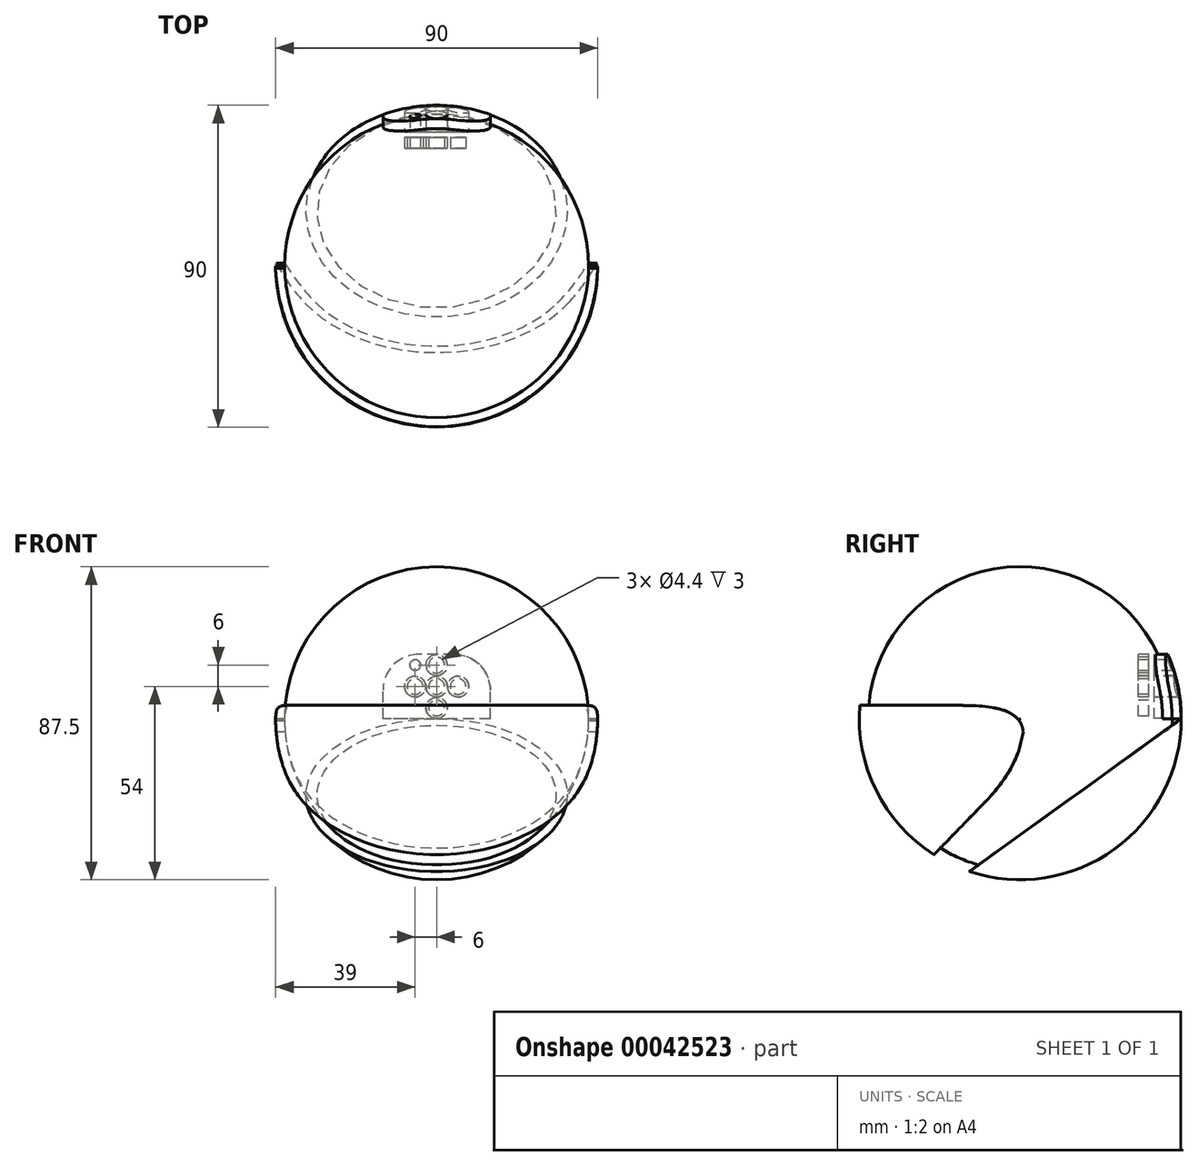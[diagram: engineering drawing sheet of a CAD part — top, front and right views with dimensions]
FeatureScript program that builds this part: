
annotation { "Feature Type Name" : "Feature", "Feature Type Description" : "" }
export const myFeature = defineFeature(function(context is Context, id is Id, definition is map)
    precondition{}
    {
        {
            var Q0;
            Q0=qCreatedBy(makeId("Right.planeOp"),FACE);
            var sketch = newSketch(context, id + "F0", { "sketchPlane" : qUnion([Q0])});
            skArc(sketch, "E0", {"start": v(40, 0) * mm, "mid": v(38.33, 11.42) * mm, "end": v(33.48, 21.9) * mm});
            skLineSegment(sketch, "E1", {"start": v(0, -40) * mm, "end": v(0, 40) * mm, "construction": true});
            skLineSegment(sketch, "E2", {"start": v(-40, 0) * mm, "end": v(40, 0) * mm, "construction": true});
            skPoint(sketch, "E3", {"position": v(33.48, 21.9) * mm});
            skPoint(sketch, "E4", {"position": v(-21.9, -33.48) * mm});
            skLineSegment(sketch, "E5", {"start": v(-21.9, -33.48) * mm, "end": v(33.48, 21.9) * mm, "construction": true});
            skPoint(sketch, "E6", {"position": v(12.26, 0.68) * mm});
            skPoint(sketch, "E7", {"position": v(-7.75, -19.33) * mm});
            skFitSpline(sketch, "E8", {"points": [v(-7.75, -19.33) * mm, v(4.22, 8.7) * mm], "startDerivative": vector(26.03, 26.03) * mm, "endDerivative": vector(-1.06, 47.13) * mm});
            skFitSpline(sketch, "E9", {"points": [v(33.48, 21.9) * mm, v(12.36, 15.68) * mm], "startDerivative": vector(-15.28, -15.28) * mm, "endDerivative": vector(-38.84, 5.85) * mm});
            skArc(sketch, "E10.trimOffspring", {"start": v(20.07, 15.1) * mm, "mid": v(11.15, 14.38) * mm, "end": v(4.22, 8.7) * mm});
            skLineSegment(sketch, "E11", {"start": v(33.48, 21.9) * mm, "end": v(40, 21.9) * mm});
            skLineSegment(sketch, "E12", {"start": v(40, 0) * mm, "end": v(40, 21.9) * mm});
            skCircle(sketch, "E13", {"center": v(0, 0) * mm, "radius": 40 * mm, "construction": true});
            skPoint(sketch, "E14", {"position": v(0, -32.17) * mm});
            skPoint(sketch, "E15", {"position": v(40, 0) * mm});
            skLineSegment(sketch, "E16", {"start": v(-21.9, -33.48) * mm, "end": v(-14.82, -40.55) * mm});
            skLineSegment(sketch, "E17", {"start": v(-14.82, -40.55) * mm, "end": v(40, 0) * mm});
            skLineSegment(sketch, "E18", {"start": v(-14.82, -40.55) * mm, "end": v(-21.9, -40.55) * mm});
            skLineSegment(sketch, "E19", {"start": v(-21.9, -33.48) * mm, "end": v(-21.9, -40.55) * mm});
            skLineSegment(sketch, "E20", {"start": v(-21.9, -33.48) * mm, "end": v(-7.75, -19.33) * mm});
            skPoint(sketch, "E21", {"position": v(-40, 0) * mm});
            skLineSegment(sketch, "E22", {"start": v(16.76, 0.47) * mm, "end": v(-57.16, 13.5) * mm, "construction": true});
            skLineSegment(sketch, "E23", {"start": v(4.13, 2.7) * mm, "end": v(-38.67, 10.24) * mm});
            skLineSegment(sketch, "E24", {"start": v(-38.67, 10.24) * mm, "end": v(-36.4, 16.58) * mm});
            skLineSegment(sketch, "E25", {"start": v(-36.4, 16.58) * mm, "end": v(-28.73, 27.84) * mm});
            skLineSegment(sketch, "E26", {"start": v(-28.73, 27.84) * mm, "end": v(-14.77, 37.17) * mm});
            skLineSegment(sketch, "E27", {"start": v(-14.77, 37.17) * mm, "end": v(5, 39.69) * mm});
            skLineSegment(sketch, "E28", {"start": v(5, 39.69) * mm, "end": v(27.43, 29.12) * mm});
            skLineSegment(sketch, "E29", {"start": v(27.43, 29.12) * mm, "end": v(33.48, 21.9) * mm});
            skSolve(sketch);
        }
        {
            var Q0;
            Q0=qCreatedBy(makeId("Top.planeOp"),FACE);
            var sketch = newSketch(context, id + "F1", { "sketchPlane" : qUnion([Q0])});
            skArc(sketch, "E30", {"start": v(42.5, 0) * mm, "mid": v(0, 42.5) * mm, "end": v(-42.5, 0) * mm});
            skArc(sketch, "E31", {"start": v(45, 0) * mm, "mid": v(0, 45) * mm, "end": v(-45, 0) * mm});
            skLineSegment(sketch, "E32", {"start": v(16.73, 41.77) * mm, "end": v(7.83, 41.77) * mm});
            skLineSegment(sketch, "E33.trimOffspring", {"start": v(-7.83, 41.77) * mm, "end": v(-16.73, 41.77) * mm});
            skLineSegment(sketch, "E34", {"start": v(45, 0) * mm, "end": v(-45, 0) * mm});
            skSolve(sketch);
        }
        {
            var Q0;
            Q0=qCreatedBy(makeId("Right.planeOp"),FACE);
            cPlane(context, id + "F2", {"entities" : qUnion([Q0]), "cplaneType" : CPlaneType.OFFSET, "offset" : 46.5 * mm, "width" : 150 * mm, "height" : 150 * mm});
        }
        {
            var Q0;
            Q0=qCreatedBy(id+"F2.planeOp",FACE);
            var sketch = newSketch(context, id + "F3", { "sketchPlane" : qUnion([Q0])});
            skPoint(sketch, "E35", {"position": v(-24.55, -38.44) * mm});
            skPoint(sketch, "E36", {"position": v(37.7, 24.87) * mm});
            skPoint(sketch, "E37", {"position": v(45, 0) * mm});
            skPoint(sketch, "E38", {"position": v(-14.2, -42.7) * mm});
            skArc(sketch, "E39", {"start": v(16.05, 18.74) * mm, "mid": v(5.9, 14.39) * mm, "end": v(1.48, 4.27) * mm});
            skFitSpline(sketch, "E40", {"points": [v(-10.32, -23.8) * mm, v(1.48, 4.27) * mm], "startDerivative": vector(30.96, 31.84) * mm, "endDerivative": vector(1.06, 30.08) * mm});
            skFitSpline(sketch, "E41", {"points": [v(37.7, 24.87) * mm, v(16.05, 18.74) * mm], "startDerivative": vector(-20.08, -19.99) * mm, "endDerivative": vector(-31.5, -0.88) * mm});
            skLineSegment(sketch, "E42.trimOffspring", {"start": v(-10.32, -23.8) * mm, "end": v(-24.55, -38.44) * mm});
            skLineSegment(sketch, "E43", {"start": v(-14.2, -42.7) * mm, "end": v(45, 0) * mm});
            skCircle(sketch, "E44", {"center": v(0, 0) * mm, "radius": 69 * mm});
            skCircle(sketch, "E45", {"center": v(0, 0) * mm, "radius": 45 * mm});
            skLineSegment(sketch, "E46", {"start": v(-14.2, -42.7) * mm, "end": v(-24.55, -42.7) * mm});
            skLineSegment(sketch, "E47", {"start": v(-24.55, -38.44) * mm, "end": v(-24.55, -42.7) * mm});
            skCircle(sketch, "E48", {"center": v(16.47, 3.74) * mm, "radius": 2.2 * mm});
            skCircle(sketch, "E49", {"center": v(16.47, 3.74) * mm, "radius": 3 * mm});
            skFitSpline(sketch, "E50", {"points": [v(0.83, -3.6) * mm, v(-20.15, 3.74) * mm], "startDerivative": vector(-2.48, 22) * mm, "endDerivative": vector(-29.81, 0) * mm});
            skLineSegment(sketch, "E51.trimOffspring", {"start": v(-20.15, 3.74) * mm, "end": v(-44.84, 3.74) * mm});
            skSolve(sketch);
        }
        {
            var Q0;
            {var subQ5=sQuery(id+"F1.wireOp",EDGE,"E33.trimOffspring");Q0=makeQuery(id+"F1.imprint","IMPRINT",FACE,{"disambiguationData":[TD([[makeQuery(id+"F1.imprint","IMPRINT",EDGE,{"derivedFrom":subQ5}),1.0]])]});}
            var Q1;
            {var subQ1=sQuery(id+"F1.wireOp",EDGE,"E32");Q1=makeQuery(id+"F1.imprint","IMPRINT",FACE,{"disambiguationData":[TD([[makeQuery(id+"F1.imprint","IMPRINT",EDGE,{"derivedFrom":subQ1}),-1.0]])]});}
            var Q2;
            {var subQ5=sQuery(id+"F1.wireOp",EDGE,"E32");Q2=makeQuery(id+"F1.imprint","IMPRINT",FACE,{"disambiguationData":[TD([[makeQuery(id+"F1.imprint","IMPRINT",EDGE,{"derivedFrom":subQ5}),1.0]])]});}
            var Q3;
            Q3=sQuery(id+"F1.wireOp",EDGE,"E34");
            revolve(context, id + "F4", {"entities" : qUnion([Q0, Q1, Q2]), "axis" : qUnion([Q3]), "revolveType" : RevolveType.TWO_DIRECTIONS, "angle" : 125 * degree, "angleBack" : 150 * degree});
        }
        {
            var Q0;
            {var subQ1=sQuery(id+"F3.wireOp",EDGE,"E43");Q0=makeQuery(id+"F3.imprint","IMPRINT",FACE,{"disambiguationData":[TD([[makeQuery(id+"F3.imprint","IMPRINT",EDGE,{"derivedFrom":subQ1}),-1.0]])]});}
            var Q1;
            Q1=makeQuery(id+"F3.imprint","IMPRINT",FACE,{"disambiguationData":[TD([[makeQuery(id+"F3.imprint","IMPRINT",EDGE,{"derivedFrom":sQuery(id+"F3.wireOp",EDGE,"E44")}),1.0]])]});
            var Q2;
            {var subQ0=sQuery(id+"F3.wireOp",EDGE,"E50");Q2=makeQuery(id+"F3.imprint","IMPRINT",FACE,{"disambiguationData":[TD([[makeQuery(id+"F3.imprint","IMPRINT",EDGE,{"derivedFrom":subQ0}),1.0]])]});}
            extrude(context, id + "F5", {"entities" : qUnion([Q0, Q1, Q2]), "operationType" : NewBodyOperationType.REMOVE, "endBound" : BoundingType.THROUGH_ALL, "oppositeDirection" : true, "depth" : 25 * mm, "offsetDistance" : 25 * mm});
        }
        {
            var Q0;
            Q0=makeQuery(id+"F3.imprint","IMPRINT",FACE,{"disambiguationData":[TD([[makeQuery(id+"F3.imprint","IMPRINT",EDGE,{"derivedFrom":sQuery(id+"F3.wireOp",EDGE,"E39")}),-1.0]])]});
            extrude(context, id + "F6", {"entities" : qUnion([Q0]), "operationType" : NewBodyOperationType.REMOVE, "endBound" : BoundingType.THROUGH_ALL, "depth" : 25 * mm});
        }
        {
            var Q0;
            Q0=qCreatedBy(makeId("Front.planeOp"),FACE);
            cPlane(context, id + "F7", {"entities" : qUnion([Q0]), "cplaneType" : CPlaneType.OFFSET, "offset" : 38 * mm, "oppositeDirection" : true, "width" : 150 * mm, "height" : 150 * mm});
        }
        {
            var Q0;
            Q0=qCreatedBy(id+"F7.planeOp",FACE);
            var sketch = newSketch(context, id + "F8", { "sketchPlane" : qUnion([Q0])});
            skLineSegment(sketch, "E52", {"start": v(0, 0) * mm, "end": v(15, 0) * mm});
            skLineSegment(sketch, "E53", {"start": v(15, 0) * mm, "end": v(15, 18) * mm});
            skLineSegment(sketch, "E54", {"start": v(15, 18) * mm, "end": v(0, 18) * mm});
            skLineSegment(sketch, "E55.MirrorCS", {"start": v(-15, 18) * mm, "end": v(0, 18) * mm});
            skLineSegment(sketch, "E56.MirrorCS", {"start": v(0, 0) * mm, "end": v(-15, 0) * mm});
            skLineSegment(sketch, "E57.MirrorCS", {"start": v(-15, 0) * mm, "end": v(-15, 18) * mm});
            skSolve(sketch);
        }
        {
            var Q0;
            Q0=makeQuery(id+"F8.imprint","IMPRINT",FACE,{"disambiguationData":[TD([[makeQuery(id+"F8.imprint","IMPRINT",EDGE,{"derivedFrom":sQuery(id+"F8.wireOp",EDGE,"E52")}),1.0]])]});
            extrude(context, id + "F9", {"entities" : qUnion([Q0]), "operationType" : NewBodyOperationType.ADD, "depth" : 5 * mm});
        }
        {
            var Q0;
            Q0=makeQuery(id+"F9.opExtrude","CAP_FACE",FACE,{"disambiguationData":[OSD([sQuery(id+"F8.wireOp",EDGE,"E52"),sQuery(id+"F8.wireOp",EDGE,"E53"),sQuery(id+"F8.wireOp",EDGE,"E54"),sQuery(id+"F8.wireOp",EDGE,"E55.MirrorCS"),sQuery(id+"F8.wireOp",EDGE,"E56.MirrorCS"),sQuery(id+"F8.wireOp",EDGE,"E57.MirrorCS")])],"isStart":false});
            var sketch = newSketch(context, id + "F10", { "sketchPlane" : qUnion([Q0])});
            skLineSegment(sketch, "E58", {"start": v(0, 0) * mm, "end": v(0, 18) * mm, "construction": true});
            skLineSegment(sketch, "E59", {"start": v(-15, 9) * mm, "end": v(15, 9) * mm, "construction": true});
            skCircle(sketch, "E60", {"center": v(0, 9) * mm, "radius": 2.95 * mm});
            skCircle(sketch, "E61", {"center": v(-6, 9) * mm, "radius": 2.95 * mm});
            skCircle(sketch, "E62", {"center": v(0, 15) * mm, "radius": 2.95 * mm});
            skCircle(sketch, "E63", {"center": v(0, 15) * mm, "radius": 2.2 * mm});
            skCircle(sketch, "E64", {"center": v(0, 9) * mm, "radius": 2.2 * mm});
            skCircle(sketch, "E65", {"center": v(-6, 9) * mm, "radius": 2.2 * mm});
            skCircle(sketch, "E66.MirrorC", {"center": v(6, 9) * mm, "radius": 2.95 * mm});
            skCircle(sketch, "E67.MirrorC", {"center": v(6, 9) * mm, "radius": 2.2 * mm});
            skCircle(sketch, "E68.MirrorC", {"center": v(0, 3) * mm, "radius": 2.95 * mm});
            skCircle(sketch, "E69.MirrorC", {"center": v(0, 3) * mm, "radius": 2.2 * mm});
            skLineSegment(sketch, "E70", {"start": v(15, 8) * mm, "end": v(15, 9) * mm});
            skLineSegment(sketch, "E71", {"start": v(5, 18) * mm, "end": v(-5, 18) * mm});
            skLineSegment(sketch, "E72", {"start": v(-15, 9) * mm, "end": v(-15, 8) * mm});
            skPoint(sketch, "E73.visualSharp", {"position": v(15, 18) * mm});
            skArc(sketch, "E73.filletArc", {"start": v(15, 8) * mm, "mid": v(12.07, 15.07) * mm, "end": v(5, 18) * mm});
            skPoint(sketch, "E74.visualSharp", {"position": v(-15, 18) * mm});
            skArc(sketch, "E74.filletArc", {"start": v(-5, 18) * mm, "mid": v(-12.07, 15.07) * mm, "end": v(-15, 8) * mm});
            skLineSegment(sketch, "E75", {"start": v(0, 15) * mm, "end": v(9.62, 15) * mm, "construction": true});
            skLineSegment(sketch, "E76", {"start": v(6, 9) * mm, "end": v(6, 16.47) * mm, "construction": true});
            skPoint(sketch, "E77", {"position": v(6, 15) * mm});
            skCircle(sketch, "E78", {"center": v(6, 15) * mm, "radius": 1.5 * mm});
            skCircle(sketch, "E79.MirrorC", {"center": v(-6, 15) * mm, "radius": 1.5 * mm});
            skSolve(sketch);
        }
        {
            var Q0;
            Q0=makeQuery(id+"F9.opExtrude","SWEPT_FACE",FACE,{"disambiguationData":[OSD([sQuery(id+"F8.wireOp",EDGE,"E52"),sQuery(id+"F8.wireOp",EDGE,"E56.MirrorCS")])]});
            var sketch = newSketch(context, id + "F11", { "sketchPlane" : qUnion([Q0])});
            skLineSegment(sketch, "E80", {"start": v(0, -38) * mm, "end": v(0, -33) * mm, "construction": true});
            skPoint(sketch, "E81", {"position": v(-12, -33) * mm});
            skPoint(sketch, "E82", {"position": v(0, -36) * mm});
            skPoint(sketch, "E83", {"position": v(0, -37.5) * mm});
            skLineSegment(sketch, "E84", {"start": v(-12, -36) * mm, "end": v(-12, -37.5) * mm});
            skLineSegment(sketch, "E85", {"start": v(0, -37.5) * mm, "end": v(-12, -37.5) * mm});
            skLineSegment(sketch, "E86", {"start": v(0, -36) * mm, "end": v(-12, -36) * mm});
            skLineSegment(sketch, "E87.MirrorCS", {"start": v(0, -36) * mm, "end": v(12, -36) * mm});
            skLineSegment(sketch, "E88.MirrorCS", {"start": v(12, -36) * mm, "end": v(12, -37.5) * mm});
            skLineSegment(sketch, "E89.MirrorCS", {"start": v(0, -37.5) * mm, "end": v(12, -37.5) * mm});
            skSolve(sketch);
        }
        {
            var Q0;
            Q0=makeQuery(id+"F11.imprint","IMPRINT",FACE,{"disambiguationData":[TD([[makeQuery(id+"F11.imprint","IMPRINT",EDGE,{"derivedFrom":sQuery(id+"F11.wireOp",EDGE,"E84")}),1.0]])]});
            var Q1;
            Q1=makeQuery(id+"F4.opRevolve","SWEPT_FACE",FACE,{"disambiguationData":[OSD([sQuery(id+"F1.wireOp",EDGE,"E30")])]});
            var Q2;
            Q2=makeQuery(id+"F4.opRevolve","SWEPT_BODY",BODY,{"disambiguationData":[OSD([sQuery(id+"F1.wireOp",EDGE,"E30"),sQuery(id+"F1.wireOp",EDGE,"E31"),sQuery(id+"F1.wireOp",EDGE,"E34")])]});
            extrude(context, id + "F12", {"entities" : qUnion([Q0]), "operationType" : NewBodyOperationType.REMOVE, "endBound" : BoundingType.UP_TO_SURFACE, "oppositeDirection" : true, "endBoundEntityFace" : qUnion([Q1]), "endBoundEntityBody" : qUnion([Q2]), "depth" : 25 * mm});
        }
        {
            var Q0;
            Q0=makeQuery(id+"F10.imprint","IMPRINT",FACE,{"disambiguationData":[TD([[makeQuery(id+"F10.imprint","IMPRINT",EDGE,{"derivedFrom":sQuery(id+"F10.wireOp",EDGE,"E65")}),1.0]])]});
            var Q1;
            Q1=makeQuery(id+"F10.imprint","IMPRINT",FACE,{"disambiguationData":[TD([[makeQuery(id+"F10.imprint","IMPRINT",EDGE,{"derivedFrom":sQuery(id+"F10.wireOp",EDGE,"E63")}),1.0]])]});
            var Q2;
            Q2=makeQuery(id+"F10.imprint","IMPRINT",FACE,{"disambiguationData":[TD([[makeQuery(id+"F10.imprint","IMPRINT",EDGE,{"derivedFrom":sQuery(id+"F10.wireOp",EDGE,"E69.MirrorC")}),-1.0]])]});
            var Q3;
            Q3=makeQuery(id+"F10.imprint","IMPRINT",FACE,{"disambiguationData":[TD([[makeQuery(id+"F10.imprint","IMPRINT",EDGE,{"derivedFrom":sQuery(id+"F10.wireOp",EDGE,"E67.MirrorC")}),-1.0]])]});
            var Q4;
            Q4=makeQuery(id+"F10.imprint","IMPRINT",FACE,{"disambiguationData":[TD([[makeQuery(id+"F10.imprint","IMPRINT",EDGE,{"derivedFrom":sQuery(id+"F10.wireOp",EDGE,"E64")}),1.0]])]});
            extrude(context, id + "F13", {"entities" : qUnion([Q0, Q1, Q2, Q3, Q4]), "operationType" : NewBodyOperationType.REMOVE, "endBound" : BoundingType.UP_TO_NEXT, "oppositeDirection" : true, "depth" : 25 * mm});
        }
        {
            var Q0;
            {var subQ1=sQuery(id+"F10.wireOp",EDGE,"E74.filletArc");Q0=makeQuery(id+"F10.imprint","IMPRINT",FACE,{"disambiguationData":[TD([[makeQuery(id+"F10.imprint","IMPRINT",EDGE,{"derivedFrom":subQ1}),-1.0]])]});}
            var Q1;
            {var subQ1=sQuery(id+"F10.wireOp",EDGE,"E73.filletArc");Q1=makeQuery(id+"F10.imprint","IMPRINT",FACE,{"disambiguationData":[TD([[makeQuery(id+"F10.imprint","IMPRINT",EDGE,{"derivedFrom":subQ1}),-1.0]])]});}
            var Q2;
            {var subQ0=sQuery(id+"F1.wireOp",EDGE,"E30");Q2=makeQuery(id+"F12.boolean.opBoolean","MERGE",FACE,{"derivedFrom":[makeQuery(id+"F4.opRevolve","SWEPT_FACE",FACE,{"disambiguationData":[OSD([subQ0])]}),makeQuery(id+"F12.opExtrude","CAP_FACE",FACE,{"disambiguationData":[OSD([subQ0])],"isStart":false})]});}
            extrude(context, id + "F14", {"entities" : qUnion([Q0, Q1]), "operationType" : NewBodyOperationType.REMOVE, "endBound" : BoundingType.UP_TO_SURFACE, "oppositeDirection" : true, "endBoundEntityFace" : qUnion([Q2]), "depth" : 25 * mm});
        }
        {
            var Q0;
            Q0=makeQuery(id+"F9.opExtrude","CAP_FACE",FACE,{"disambiguationData":[OSD([sQuery(id+"F8.wireOp",EDGE,"E52"),sQuery(id+"F8.wireOp",EDGE,"E53"),sQuery(id+"F8.wireOp",EDGE,"E54"),sQuery(id+"F8.wireOp",EDGE,"E55.MirrorCS"),sQuery(id+"F8.wireOp",EDGE,"E56.MirrorCS"),sQuery(id+"F8.wireOp",EDGE,"E57.MirrorCS")])],"isStart":true});
            extrude(context, id + "F15", {"entities" : qUnion([Q0]), "operationType" : NewBodyOperationType.ADD, "endBound" : BoundingType.UP_TO_NEXT, "depth" : 25 * mm});
        }
        {
            var Q0;
            Q0=makeQuery(id+"F10.imprint","IMPRINT",FACE,{"disambiguationData":[TD([[makeQuery(id+"F10.imprint","IMPRINT",EDGE,{"derivedFrom":sQuery(id+"F10.wireOp",EDGE,"E79.MirrorC")}),-1.0]])]});
            var Q1;
            Q1=makeQuery(id+"F10.imprint","IMPRINT",FACE,{"disambiguationData":[TD([[makeQuery(id+"F10.imprint","IMPRINT",EDGE,{"derivedFrom":sQuery(id+"F10.wireOp",EDGE,"E78")}),1.0]])]});
            extrude(context, id + "F16", {"entities" : qUnion([Q0, Q1]), "operationType" : NewBodyOperationType.REMOVE, "endBound" : BoundingType.THROUGH_ALL, "oppositeDirection" : true, "depth" : 25 * mm});
        }
    });
